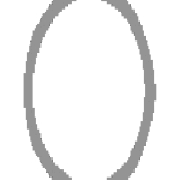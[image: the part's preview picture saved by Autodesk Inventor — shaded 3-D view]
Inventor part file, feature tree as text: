
AUTODESK INVENTOR PART (.ipt)
format: ipt  version: 2021 (Build 250183000, 183)  size: 113,152 bytes
history: native  units: in
note: dims shown in document units (in); Inventor stores cm internally (conversion verified against a paired STEP export)
features: other x4, sketch x3, plane x1
ambient origin geometry x8: Origin, YZ Plane, XZ Plane, XY Plane, X Axis, Y Axis, Z Axis, Center Point
bodies: Solid1 (feature_tree), Body (feature_tree)
feature tree (8):
  other  "Driven Length"
  other  "Frame Generator"
  other  "Start Plane"
  other  "End Plane"
  sketch  "Sketch"  dims[d2=8.0898in d4=-0.0in d5=8.0898in d6=0.12in d7=0.0in d8=90.0deg d9=8.0898in]
  sketch  "Sketch2"  dims[d0=1.0in]
  plane  "Work Plane3"
  sketch  "Sketch3"  dims[d1=0.065in]
